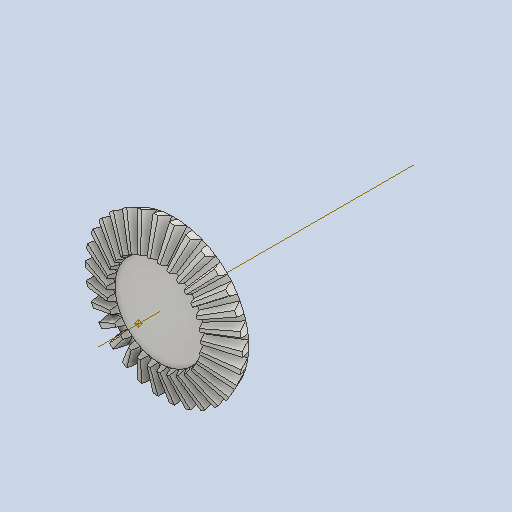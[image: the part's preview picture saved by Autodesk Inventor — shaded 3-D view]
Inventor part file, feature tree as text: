
AUTODESK INVENTOR PART (.ipt)
format: ipt  version: 2022 (Build 260153000, 153)  size: 658,944 bytes
history: native  units: in
note: dims shown in document units (in); Inventor stores cm internally (conversion verified against a paired STEP export)
features: other x30, sketch x1
ambient origin geometry x8: Origin, YZ Plane, XZ Plane, XY Plane, X Axis, Y Axis, Z Axis, Center Point
bodies: Solid1 (feature_tree)
feature tree (31):
  other  "Bevel Gear21_MIR2.ipt"
  other  "Solid1::Bevel Gear21_MIR2.ipt"
  other  "TaggingFeature1"
  other  "Teeth Body Sketch"
  other  "Start Sketch"
  other  "End Sketch"
  other  "End Sketch Right"
  other  "End Sketch Left"
  other  "Body Sketch"
  sketch  "Sketch6"  dims[d0=0.3937in d48=0.0in d49=0.0in d50=90.0deg d52=0.0in d53=0.0in d54=0.0in]
  other  "3D Sketch Right"
  other  "3D Sketch Left"
  other  "Mesh Plane"
  other  "Top Plane"
  other  "Mesh Plane2"
  other  "Tooth Plane"
  other  "End Plane"
  other  "End Plane Right"
  other  "End Plane Left"
  other  "Z Axis_1"
  other  "Top Point"
  other  "Start Point"
  other  "End Point"
  other  "Srf1"
  other  "Srf1::Derived"
  other  "Start plane iMate"
  other  "Mesh iMate2"
  other  "Axis Angle iMate"
  other  "Axis iMate"
  other  "Mesh iMate"
  other  "Intersection iMate"
